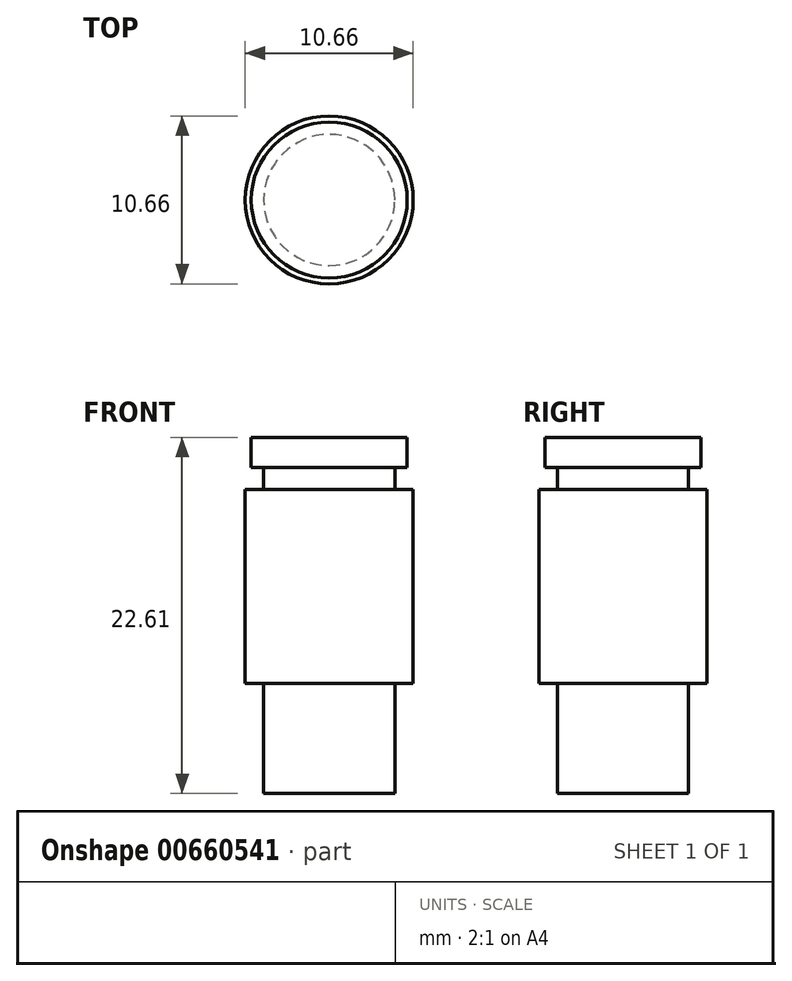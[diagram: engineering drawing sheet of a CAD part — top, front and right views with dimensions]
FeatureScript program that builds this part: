
annotation { "Feature Type Name" : "Feature", "Feature Type Description" : "" }
export const myFeature = defineFeature(function(context is Context, id is Id, definition is map)
    precondition{}
    {
        {
            var Q0;
            Q0=qCreatedBy(makeId("Front.planeOp"),FACE);
            var sketch = newSketch(context, id + "F0", { "sketchPlane" : qUnion([Q0])});
            skLineSegment(sketch, "E0", {"start": v(0, -6.48) * mm, "end": v(0, 0) * mm, "construction": true});
            skLineSegment(sketch, "E1", {"start": v(0, 0) * mm, "end": v(0, 22.6) * mm});
            skLineSegment(sketch, "E2", {"start": v(0, 22.6) * mm, "end": v(4.95, 22.6) * mm});
            skLineSegment(sketch, "E3", {"start": v(4.95, 20.7) * mm, "end": v(4.17, 20.7) * mm});
            skLineSegment(sketch, "E4", {"start": v(4.17, 19.3) * mm, "end": v(5.33, 19.3) * mm});
            skLineSegment(sketch, "E5", {"start": v(5.33, 19.3) * mm, "end": v(5.33, 6.99) * mm});
            skLineSegment(sketch, "E6", {"start": v(5.33, 6.99) * mm, "end": v(4.17, 6.99) * mm});
            skLineSegment(sketch, "E7", {"start": v(4.17, 6.99) * mm, "end": v(4.17, 0) * mm});
            skLineSegment(sketch, "E8", {"start": v(4.17, 0) * mm, "end": v(0, 0) * mm});
            skLineSegment(sketch, "E9", {"start": v(4.17, 20.7) * mm, "end": v(4.17, 19.3) * mm});
            skLineSegment(sketch, "E10", {"start": v(4.95, 22.6) * mm, "end": v(4.95, 20.7) * mm});
            skSolve(sketch);
        }
        {
            var Q0;
            Q0 = qSketchRegion(id + "F0", true);
            var Q1;
            Q1=sQuery(id+"F0.wireOp",EDGE,"E0");
            revolve(context, id + "F1", {"entities" : qUnion([Q0]), "axis" : qUnion([Q1]), "revolveType" : RevolveType.FULL});
        }
    });
